# Revit family: 66-REG PLAST ACOPLE SAN
name_source: partatom
category: Aparatos sanitarios
revit_build: Autodesk Revit 2018 (Build: 20170223_1515(x64)
units: mm (PartAtom-declared; Revit-internal decimal feet)

## family parameters
Anfitrión = Cara
Compartido = No
Corte con vacíos al cargar = No
Cota de conector redondo = Diámetro de uso
Número OmniClass = 23.45.55.00
Punto de cálculo de habitación = No
Tipo de pieza = Normal
Título OmniClass = Sanitary Faucets, Wastes

## types (1)
- 66-REG PLAST ACOPLE SAN
    Acabado = Mate
    Altura Nominal = 130.9
    Ancho Nominal = 55.7
    Características = Alta resistencia al torque, fácil instalación, resistente a la corrosión
    Caudal = Caudal máximo de 36l/min.
    Color = Blanco
    Consumo de agua = 8,3l/min.
    Cumplimiento de Norma = Cumple con norma IAPMO IGC 157
    Código de montaje = D2010
    Descripción = Plumbing Fixtures
    Descripción IFC = Regulación plástica (de 1/2” sencilla)
    Diámetro de conexión entrada = 1/2 Pulg para lavamanos y lavaplatos, 15/16 para sanitarios
    Elevación por defecto = 0 mm  [stored 0 ft]
    Fabricante = www.corona.com.co
    Forma = Cilíndrica
    Logitud Nominal = 111.1
    Material Acabado = Plástico Corona Blanco Plomeria
    Material de Fabricación = Plástico
    Nombre = Regulación plástica
    Nombre del Fabricante = Corona
    Número Modelo = 967350001
    Presión Máxima = 125 psi.
    Presión mínima = 20 psi.
    Requerimientos Accesibilidad = Manual
    Responsable Garantías Partes = www.corona.com.co
    Tamaño = 64 x 55,7 x 111,1
    Tipo de Activo = Fijo
    Tráfico = Residencial
    Vida útil = unidad de cierre 2000
    Vida útil unidad = Ciclos

note: [stored X ft] marks values corroborated as IEEE doubles in the binary element streams (Revit-internal decimal feet)

## geometry (parser evidence)
native form markers: Sweep x2
no freeform markers — native parametric forms only
